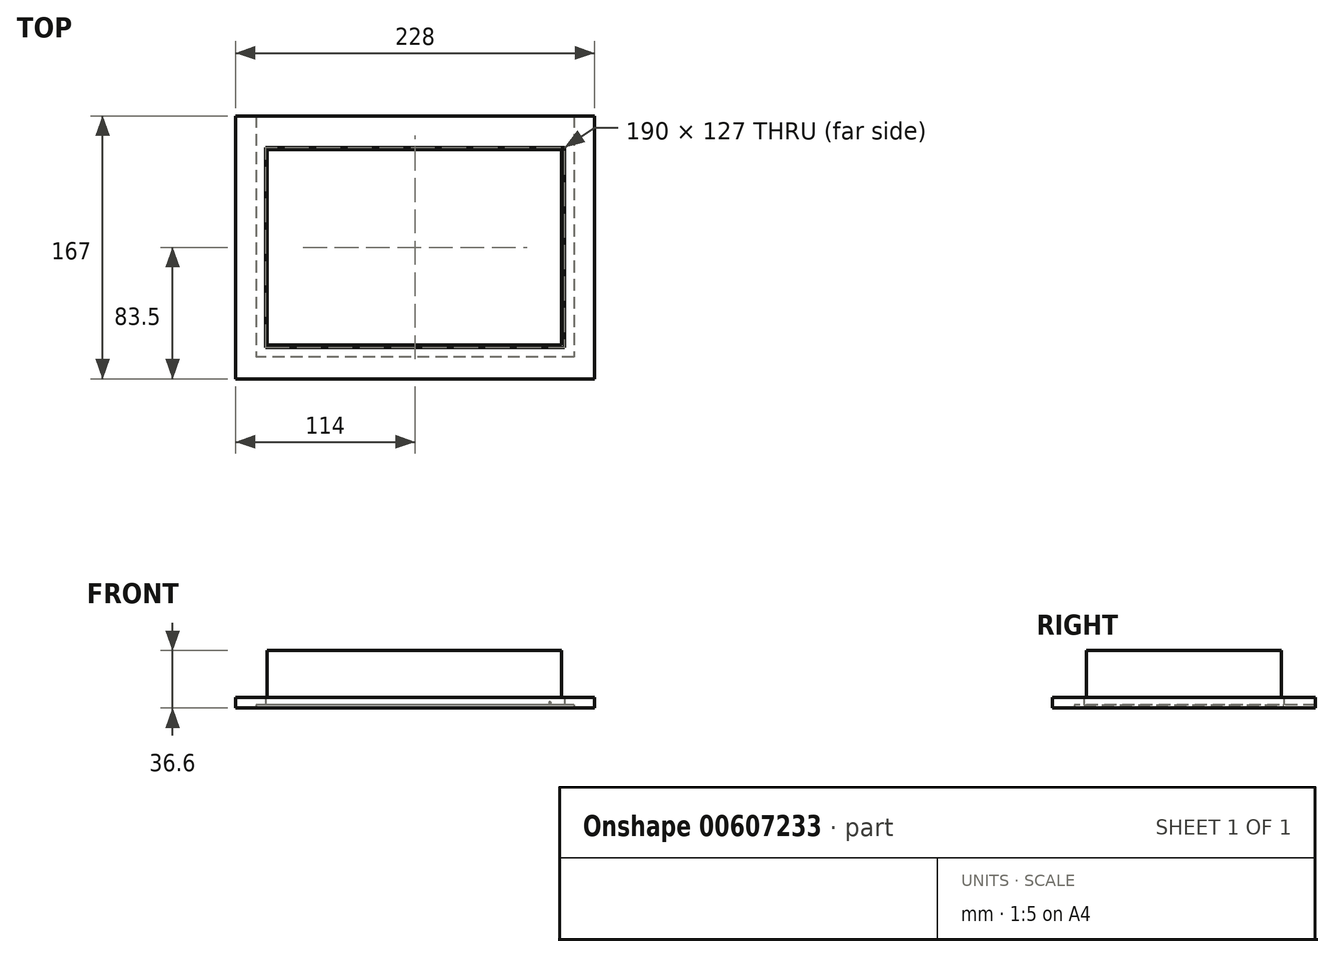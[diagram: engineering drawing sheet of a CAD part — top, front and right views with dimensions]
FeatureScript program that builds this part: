
annotation { "Feature Type Name" : "Feature", "Feature Type Description" : "" }
export const myFeature = defineFeature(function(context is Context, id is Id, definition is map)
    precondition{}
    {
        {
            var Q0;
            Q0=qCreatedBy(makeId("Top.planeOp"),FACE);
            var sketch = newSketch(context, id + "F0", { "sketchPlane" : qUnion([Q0])});
            skLineSegment(sketch, "E0.bottom", {"start": v(114, 83.5) * mm, "end": v(-114, 83.5) * mm});
            skLineSegment(sketch, "E0.top", {"start": v(114, -83.5) * mm, "end": v(-114, -83.5) * mm});
            skLineSegment(sketch, "E0.left", {"start": v(114, 83.5) * mm, "end": v(114, -83.5) * mm});
            skLineSegment(sketch, "E0.right", {"start": v(-114, 83.5) * mm, "end": v(-114, -83.5) * mm});
            skPoint(sketch, "E0.middle", {"position": v(0, 0) * mm});
            skLineSegment(sketch, "E1.bottom", {"start": v(-95, 63.5) * mm, "end": v(95, 63.5) * mm});
            skLineSegment(sketch, "E1.top", {"start": v(-95, -63.5) * mm, "end": v(95, -63.5) * mm});
            skLineSegment(sketch, "E1.left", {"start": v(-95, 63.5) * mm, "end": v(-95, -63.5) * mm});
            skLineSegment(sketch, "E1.right", {"start": v(95, 63.5) * mm, "end": v(95, -63.5) * mm});
            skSolve(sketch);
        }
        {
            var Q0;
            Q0=makeQuery(id+"F0.imprint","IMPRINT",FACE,{"disambiguationData":[TD([[makeQuery(id+"F0.imprint","IMPRINT",EDGE,{"derivedFrom":sQuery(id+"F0.wireOp",EDGE,"E0.bottom")}),1.0]])]});
            extrude(context, id + "F1", {"entities" : qUnion([Q0]), "depth" : 6.6 * mm, "offsetDistance" : 25 * mm});
        }
        {
            var Q0;
            Q0=makeQuery(id+"F1.opExtrude","CAP_FACE",FACE,{"disambiguationData":[OSD([sQuery(id+"F0.wireOp",EDGE,"E0.bottom"),sQuery(id+"F0.wireOp",EDGE,"E0.top"),sQuery(id+"F0.wireOp",EDGE,"E0.left"),sQuery(id+"F0.wireOp",EDGE,"E0.right"),sQuery(id+"F0.wireOp",EDGE,"E1.bottom"),sQuery(id+"F0.wireOp",EDGE,"E1.top"),sQuery(id+"F0.wireOp",EDGE,"E1.left"),sQuery(id+"F0.wireOp",EDGE,"E1.right")])],"isStart":true});
            var sketch = newSketch(context, id + "F2", { "sketchPlane" : qUnion([Q0])});
            skLineSegment(sketch, "E2.bottom", {"start": v(101, -83.5) * mm, "end": v(-101, -83.5) * mm});
            skLineSegment(sketch, "E2.top", {"start": v(101, 69.5) * mm, "end": v(-101, 69.5) * mm});
            skLineSegment(sketch, "E2.left", {"start": v(101, -83.5) * mm, "end": v(101, 69.5) * mm});
            skLineSegment(sketch, "E2.right", {"start": v(-101, -83.5) * mm, "end": v(-101, 69.5) * mm});
            skSolve(sketch);
        }
        {
            var Q0;
            Q0 = qSketchRegion(id + "F2", true);
            extrude(context, id + "F3", {"entities" : qUnion([Q0]), "operationType" : NewBodyOperationType.REMOVE, "oppositeDirection" : true, "depth" : 2 * mm, "offsetDistance" : 25 * mm});
        }
        {
            var Q0;
            Q0=makeQuery(id+"F3.boolean.opBoolean","COPY",FACE,{"derivedFrom":makeQuery(id+"F3.opExtrude","CAP_FACE",FACE,{"disambiguationData":[OSD([sQuery(id+"F2.wireOp",EDGE,"E2.bottom"),sQuery(id+"F2.wireOp",EDGE,"E2.top"),sQuery(id+"F2.wireOp",EDGE,"E2.left"),sQuery(id+"F2.wireOp",EDGE,"E2.right")])],"isStart":false})});
            var sketch = newSketch(context, id + "F4", { "sketchPlane" : qUnion([Q0])});
            skCircle(sketch, "E3", {"center": v(85.6, -83.5) * mm, "radius": 0.4 * mm});
            skSolve(sketch);
        }
        {
            var Q0;
            Q0 = qSketchRegion(id + "F4", true);
            extrude(context, id + "F5", {"entities" : qUnion([Q0]), "operationType" : NewBodyOperationType.REMOVE, "oppositeDirection" : true, "depth" : 2 * mm, "offsetDistance" : 25 * mm});
        }
        {
            var Q0;
            Q0=makeQuery(id+"F1.opExtrude","CAP_FACE",FACE,{"disambiguationData":[OSD([sQuery(id+"F0.wireOp",EDGE,"E0.bottom"),sQuery(id+"F0.wireOp",EDGE,"E0.top"),sQuery(id+"F0.wireOp",EDGE,"E0.left"),sQuery(id+"F0.wireOp",EDGE,"E0.right"),sQuery(id+"F0.wireOp",EDGE,"E1.bottom"),sQuery(id+"F0.wireOp",EDGE,"E1.top"),sQuery(id+"F0.wireOp",EDGE,"E1.left"),sQuery(id+"F0.wireOp",EDGE,"E1.right")])],"isStart":false});
            var sketch = newSketch(context, id + "F6", { "sketchPlane" : qUnion([Q0])});
            skLineSegment(sketch, "E4.bottom", {"start": v(-74.36, 45.15) * mm, "end": v(76.35, 45.15) * mm});
            skLineSegment(sketch, "E4.top", {"start": v(-74.36, -47.87) * mm, "end": v(76.35, -47.87) * mm});
            skLineSegment(sketch, "E4.left", {"start": v(-74.36, 45.15) * mm, "end": v(-74.36, -47.87) * mm});
            skLineSegment(sketch, "E4.right", {"start": v(76.35, 45.15) * mm, "end": v(76.35, -47.87) * mm});
            skCircle(sketch, "E5", {"center": v(-95, 65.5) * mm, "radius": 1.5 * mm});
            skCircle(sketch, "E6", {"center": v(-86.7, 65.5) * mm, "radius": 1.5 * mm});
            skCircle(sketch, "E7", {"center": v(-78.4, 65.5) * mm, "radius": 1.5 * mm});
            skCircle(sketch, "E8", {"center": v(-70.1, 65.5) * mm, "radius": 1.5 * mm});
            skCircle(sketch, "E9", {"center": v(-61.8, 65.5) * mm, "radius": 1.5 * mm});
            skCircle(sketch, "E10", {"center": v(-53.5, 65.5) * mm, "radius": 1.5 * mm});
            skCircle(sketch, "E11", {"center": v(-45.2, 65.5) * mm, "radius": 1.5 * mm});
            skCircle(sketch, "E12", {"center": v(-36.9, 65.5) * mm, "radius": 1.5 * mm});
            skCircle(sketch, "E13", {"center": v(-28.6, 65.5) * mm, "radius": 1.5 * mm});
            skCircle(sketch, "E14", {"center": v(-20.3, 65.5) * mm, "radius": 1.5 * mm});
            skCircle(sketch, "E15", {"center": v(-12, 65.5) * mm, "radius": 1.5 * mm});
            skCircle(sketch, "E16", {"center": v(-3.7, 65.5) * mm, "radius": 1.5 * mm});
            skCircle(sketch, "E17", {"center": v(4.6, 65.5) * mm, "radius": 1.5 * mm});
            skCircle(sketch, "E18", {"center": v(12.9, 65.5) * mm, "radius": 1.5 * mm});
            skCircle(sketch, "E19", {"center": v(21.2, 65.5) * mm, "radius": 1.5 * mm});
            skCircle(sketch, "E20", {"center": v(29.5, 65.5) * mm, "radius": 1.5 * mm});
            skCircle(sketch, "E21", {"center": v(37.8, 65.5) * mm, "radius": 1.5 * mm});
            skCircle(sketch, "E22", {"center": v(46.1, 65.5) * mm, "radius": 1.5 * mm});
            skCircle(sketch, "E23", {"center": v(54.4, 65.5) * mm, "radius": 1.5 * mm});
            skCircle(sketch, "E24", {"center": v(62.7, 65.5) * mm, "radius": 1.5 * mm});
            skCircle(sketch, "E25", {"center": v(71, 65.5) * mm, "radius": 1.5 * mm});
            skCircle(sketch, "E26", {"center": v(79.3, 65.5) * mm, "radius": 1.5 * mm});
            skCircle(sketch, "E27", {"center": v(87.6, 65.5) * mm, "radius": 1.5 * mm});
            skCircle(sketch, "E28", {"center": v(95.9, 65.5) * mm, "radius": 1.5 * mm});
            skCircle(sketch, "E29", {"center": v(-95, 53.67) * mm, "radius": 1.5 * mm});
            skCircle(sketch, "E30", {"center": v(-95, 41.84) * mm, "radius": 1.5 * mm});
            skCircle(sketch, "E31", {"center": v(-95, 30) * mm, "radius": 1.5 * mm});
            skCircle(sketch, "E32", {"center": v(-95, 18.18) * mm, "radius": 1.5 * mm});
            skCircle(sketch, "E33", {"center": v(-95, 6.35) * mm, "radius": 1.5 * mm});
            skCircle(sketch, "E34", {"center": v(-95, -5.48) * mm, "radius": 1.5 * mm});
            skCircle(sketch, "E35", {"center": v(-95, -17.31) * mm, "radius": 1.5 * mm});
            skCircle(sketch, "E36", {"center": v(-95, -29.14) * mm, "radius": 1.5 * mm});
            skCircle(sketch, "E37", {"center": v(-95, -40.97) * mm, "radius": 1.5 * mm});
            skCircle(sketch, "E38", {"center": v(-95, -52.8) * mm, "radius": 1.5 * mm});
            skCircle(sketch, "E39", {"center": v(-95, -64.63) * mm, "radius": 1.5 * mm});
            skSolve(sketch);
        }
        {
            var Q0;
            Q0=makeQuery(id+"F6.imprint","IMPRINT",FACE,{"disambiguationData":[TD([[makeQuery(id+"F6.imprint","IMPRINT",EDGE,{"derivedFrom":sQuery(id+"F6.wireOp",EDGE,"E4.bottom")}),-1.0]])]});
            var sketch = newSketch(context, id + "F7", { "sketchPlane" : qUnion([Q0])});
            skLineSegment(sketch, "E40.bottom", {"start": v(-93.9, 61.99) * mm, "end": v(93.1, 61.99) * mm});
            skLineSegment(sketch, "E40.top", {"start": v(-93.9, -62.01) * mm, "end": v(93.1, -62.01) * mm});
            skLineSegment(sketch, "E40.left", {"start": v(-93.9, 61.99) * mm, "end": v(-93.9, -62.01) * mm});
            skLineSegment(sketch, "E40.right", {"start": v(93.1, 61.99) * mm, "end": v(93.1, -62.01) * mm});
            skSolve(sketch);
        }
        {
            var Q0;
            Q0 = qSketchRegion(id + "F7", true);
            extrude(context, id + "F8", {"entities" : qUnion([Q0]), "depth" : 30 * mm, "offsetDistance" : 25 * mm});
        }
    });
